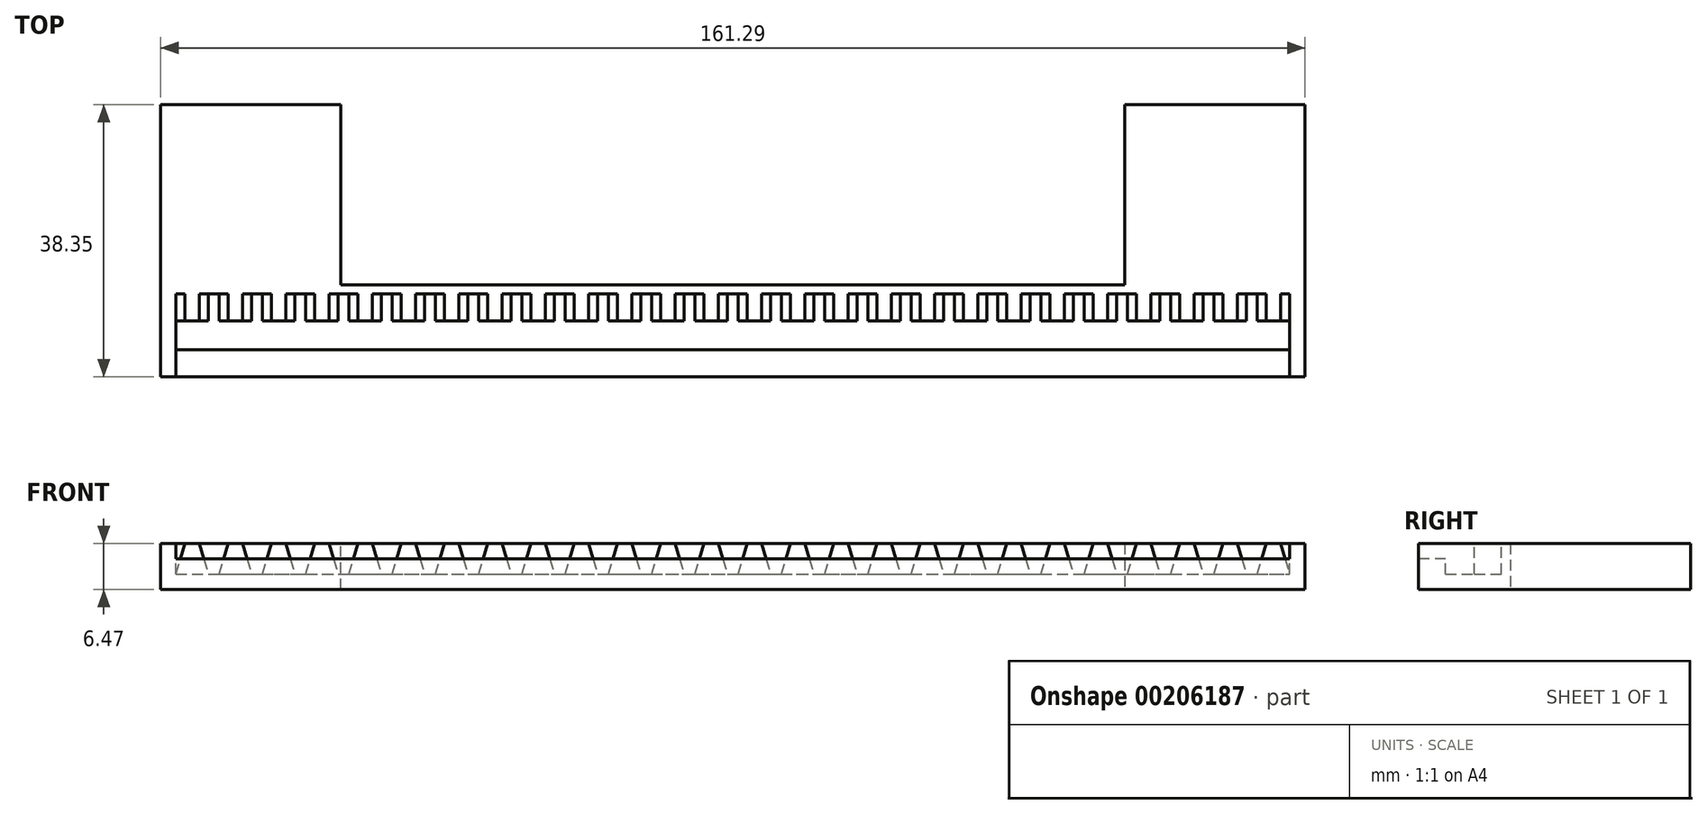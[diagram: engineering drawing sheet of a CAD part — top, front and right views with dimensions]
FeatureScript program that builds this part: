
annotation { "Feature Type Name" : "Feature", "Feature Type Description" : "" }
export const myFeature = defineFeature(function(context is Context, id is Id, definition is map)
    precondition{}
    {
        {
            var Q0;
            Q0=qCreatedBy(makeId("Front.planeOp"),FACE);
            var sketch = newSketch(context, id + "F0", { "sketchPlane" : qUnion([Q0])});
            skLineSegment(sketch, "E0.top", {"start": v(-38.44, 16.9) * mm, "end": v(33.18, 16.9) * mm});
            skLineSegment(sketch, "E0.left", {"start": v(-38.44, 14.74) * mm, "end": v(-38.44, 16.9) * mm});
            skLineSegment(sketch, "E1", {"start": v(-38.44, 16.9) * mm, "end": v(-37.17, 21.21) * mm});
            skLineSegment(sketch, "E2", {"start": v(-37.17, 21.21) * mm, "end": v(-35.14, 21.21) * mm});
            skLineSegment(sketch, "E3", {"start": v(-35.14, 21.21) * mm, "end": v(-33.87, 16.9) * mm});
            skLineSegment(sketch, "E4", {"start": v(-38.44, 16.9) * mm, "end": v(-33.87, 16.9) * mm});
            skLineSegment(sketch, "E5", {"start": v(-36.16, 21.21) * mm, "end": v(-36.16, 16.9) * mm, "construction": true});
            skLineSegment(sketch, "E6.1.0.0", {"start": v(-29.05, 21.21) * mm, "end": v(-27.78, 16.9) * mm});
            skLineSegment(sketch, "E6.1.0.1", {"start": v(-32.35, 16.9) * mm, "end": v(-31.08, 21.21) * mm});
            skLineSegment(sketch, "E6.1.0.2", {"start": v(-31.08, 21.21) * mm, "end": v(-29.05, 21.21) * mm});
            skLineSegment(sketch, "E6.2.0.0", {"start": v(-22.95, 21.21) * mm, "end": v(-21.68, 16.9) * mm});
            skLineSegment(sketch, "E6.2.0.1", {"start": v(-26.25, 16.9) * mm, "end": v(-24.98, 21.21) * mm});
            skLineSegment(sketch, "E6.2.0.2", {"start": v(-24.98, 21.21) * mm, "end": v(-22.95, 21.21) * mm});
            skLineSegment(sketch, "E6.3.0.0", {"start": v(-16.85, 21.21) * mm, "end": v(-15.58, 16.9) * mm});
            skLineSegment(sketch, "E6.3.0.1", {"start": v(-20.16, 16.9) * mm, "end": v(-18.89, 21.21) * mm});
            skLineSegment(sketch, "E6.3.0.2", {"start": v(-18.89, 21.21) * mm, "end": v(-16.85, 21.21) * mm});
            skLineSegment(sketch, "E6.4.0.0", {"start": v(-10.76, 21.21) * mm, "end": v(-9.49, 16.9) * mm});
            skLineSegment(sketch, "E6.4.0.1", {"start": v(-14.06, 16.9) * mm, "end": v(-12.8, 21.21) * mm});
            skLineSegment(sketch, "E6.4.0.2", {"start": v(-12.8, 21.21) * mm, "end": v(-10.76, 21.21) * mm});
            skLineSegment(sketch, "E6.5.0.0", {"start": v(-4.66, 21.21) * mm, "end": v(-3.4, 16.9) * mm});
            skLineSegment(sketch, "E6.5.0.1", {"start": v(-7.96, 16.9) * mm, "end": v(-6.7, 21.21) * mm});
            skLineSegment(sketch, "E6.5.0.2", {"start": v(-6.7, 21.21) * mm, "end": v(-4.66, 21.21) * mm});
            skLineSegment(sketch, "E6.6.0.0", {"start": v(1.43, 21.21) * mm, "end": v(2.7, 16.9) * mm});
            skLineSegment(sketch, "E6.6.0.1", {"start": v(-1.87, 16.9) * mm, "end": v(-0.6, 21.21) * mm});
            skLineSegment(sketch, "E6.6.0.2", {"start": v(-0.6, 21.21) * mm, "end": v(1.43, 21.21) * mm});
            skLineSegment(sketch, "E6.7.0.0", {"start": v(7.53, 21.21) * mm, "end": v(8.8, 16.9) * mm});
            skLineSegment(sketch, "E6.7.0.1", {"start": v(4.23, 16.9) * mm, "end": v(5.5, 21.21) * mm});
            skLineSegment(sketch, "E6.7.0.2", {"start": v(5.5, 21.21) * mm, "end": v(7.53, 21.21) * mm});
            skLineSegment(sketch, "E6.8.0.0", {"start": v(13.63, 21.21) * mm, "end": v(14.9, 16.9) * mm});
            skLineSegment(sketch, "E6.8.0.1", {"start": v(10.32, 16.9) * mm, "end": v(11.6, 21.21) * mm});
            skLineSegment(sketch, "E6.8.0.2", {"start": v(11.6, 21.21) * mm, "end": v(13.63, 21.21) * mm});
            skLineSegment(sketch, "E6.9.0.0", {"start": v(19.72, 21.21) * mm, "end": v(21, 16.9) * mm});
            skLineSegment(sketch, "E6.9.0.1", {"start": v(16.42, 16.9) * mm, "end": v(17.69, 21.21) * mm});
            skLineSegment(sketch, "E6.9.0.2", {"start": v(17.69, 21.21) * mm, "end": v(19.72, 21.21) * mm});
            skLineSegment(sketch, "E6.10.0.0", {"start": v(25.82, 21.21) * mm, "end": v(27.09, 16.9) * mm});
            skLineSegment(sketch, "E6.10.0.1", {"start": v(22.52, 16.9) * mm, "end": v(23.79, 21.21) * mm});
            skLineSegment(sketch, "E6.10.0.2", {"start": v(23.79, 21.21) * mm, "end": v(25.82, 21.21) * mm});
            skLineSegment(sketch, "E6.11.0.0", {"start": v(31.91, 21.21) * mm, "end": v(33.18, 16.9) * mm});
            skLineSegment(sketch, "E6.11.0.1", {"start": v(28.61, 16.9) * mm, "end": v(29.88, 21.21) * mm});
            skLineSegment(sketch, "E6.11.0.2", {"start": v(29.88, 21.21) * mm, "end": v(31.91, 21.21) * mm});
            skLineSegment(sketch, "E6.direction1", {"start": v(-38.44, 16.9) * mm, "end": v(-32.35, 16.9) * mm, "construction": true});
            skPoint(sketch, "E7.centerSnap0", {"position": v(-38.44, 15.82) * mm});
            skLineSegment(sketch, "E8.0.12.0", {"start": v(38, 21.21) * mm, "end": v(39.28, 16.9) * mm});
            skLineSegment(sketch, "E8.3.12.0", {"start": v(34.7, 16.9) * mm, "end": v(35.98, 21.21) * mm});
            skLineSegment(sketch, "E8.6.12.0", {"start": v(35.98, 21.21) * mm, "end": v(38, 21.21) * mm});
            skLineSegment(sketch, "E8.0.13.0", {"start": v(44.1, 21.21) * mm, "end": v(45.38, 16.9) * mm});
            skLineSegment(sketch, "E8.3.13.0", {"start": v(40.8, 16.9) * mm, "end": v(42.07, 21.21) * mm});
            skLineSegment(sketch, "E8.6.13.0", {"start": v(42.07, 21.21) * mm, "end": v(44.1, 21.21) * mm});
            skLineSegment(sketch, "E8.0.14.0", {"start": v(50.2, 21.21) * mm, "end": v(51.47, 16.9) * mm});
            skLineSegment(sketch, "E8.3.14.0", {"start": v(46.9, 16.9) * mm, "end": v(48.17, 21.21) * mm});
            skLineSegment(sketch, "E8.6.14.0", {"start": v(48.17, 21.21) * mm, "end": v(50.2, 21.21) * mm});
            skLineSegment(sketch, "E8.0.15.0", {"start": v(56.3, 21.21) * mm, "end": v(57.57, 16.9) * mm});
            skLineSegment(sketch, "E8.3.15.0", {"start": v(53, 16.9) * mm, "end": v(54.27, 21.21) * mm});
            skLineSegment(sketch, "E8.6.15.0", {"start": v(54.27, 21.21) * mm, "end": v(56.3, 21.21) * mm});
            skLineSegment(sketch, "E8.0.16.0", {"start": v(62.4, 21.21) * mm, "end": v(63.66, 16.9) * mm});
            skLineSegment(sketch, "E8.3.16.0", {"start": v(59.1, 16.9) * mm, "end": v(60.36, 21.21) * mm});
            skLineSegment(sketch, "E8.6.16.0", {"start": v(60.36, 21.21) * mm, "end": v(62.4, 21.21) * mm});
            skLineSegment(sketch, "E8.0.17.0", {"start": v(68.49, 21.21) * mm, "end": v(69.76, 16.9) * mm});
            skLineSegment(sketch, "E8.3.17.0", {"start": v(65.19, 16.9) * mm, "end": v(66.46, 21.21) * mm});
            skLineSegment(sketch, "E8.6.17.0", {"start": v(66.46, 21.21) * mm, "end": v(68.49, 21.21) * mm});
            skLineSegment(sketch, "E9.0.18.0", {"start": v(74.59, 21.21) * mm, "end": v(75.86, 16.9) * mm});
            skLineSegment(sketch, "E9.3.18.0", {"start": v(71.28, 16.9) * mm, "end": v(72.55, 21.21) * mm});
            skLineSegment(sketch, "E9.6.18.0", {"start": v(72.55, 21.21) * mm, "end": v(74.59, 21.21) * mm});
            skLineSegment(sketch, "E9.0.19.0", {"start": v(80.68, 21.21) * mm, "end": v(81.95, 16.9) * mm});
            skLineSegment(sketch, "E9.3.19.0", {"start": v(77.38, 16.9) * mm, "end": v(78.65, 21.21) * mm});
            skLineSegment(sketch, "E9.6.19.0", {"start": v(78.65, 21.21) * mm, "end": v(80.68, 21.21) * mm});
            skLineSegment(sketch, "E10.0.20.0", {"start": v(86.78, 21.21) * mm, "end": v(88.05, 16.9) * mm});
            skLineSegment(sketch, "E10.3.20.0", {"start": v(83.48, 16.9) * mm, "end": v(84.75, 21.21) * mm});
            skLineSegment(sketch, "E10.6.20.0", {"start": v(84.75, 21.21) * mm, "end": v(86.78, 21.21) * mm});
            skLineSegment(sketch, "E10.0.21.0", {"start": v(92.87, 21.21) * mm, "end": v(94.14, 16.9) * mm});
            skLineSegment(sketch, "E10.3.21.0", {"start": v(89.57, 16.9) * mm, "end": v(90.84, 21.21) * mm});
            skLineSegment(sketch, "E10.6.21.0", {"start": v(90.84, 21.21) * mm, "end": v(92.87, 21.21) * mm});
            skLineSegment(sketch, "E10.0.22.0", {"start": v(98.97, 21.21) * mm, "end": v(100.24, 16.9) * mm});
            skLineSegment(sketch, "E10.3.22.0", {"start": v(95.67, 16.9) * mm, "end": v(96.94, 21.21) * mm});
            skLineSegment(sketch, "E10.6.22.0", {"start": v(96.94, 21.21) * mm, "end": v(98.97, 21.21) * mm});
            skLineSegment(sketch, "E10.0.23.0", {"start": v(105.07, 21.21) * mm, "end": v(106.34, 16.9) * mm});
            skLineSegment(sketch, "E10.3.23.0", {"start": v(101.76, 16.9) * mm, "end": v(103.03, 21.21) * mm});
            skLineSegment(sketch, "E10.6.23.0", {"start": v(103.03, 21.21) * mm, "end": v(105.07, 21.21) * mm});
            skLineSegment(sketch, "E11.0.24.0", {"start": v(111.16, 21.21) * mm, "end": v(112.43, 16.9) * mm});
            skLineSegment(sketch, "E11.3.24.0", {"start": v(107.86, 16.9) * mm, "end": v(109.13, 21.21) * mm});
            skLineSegment(sketch, "E11.6.24.0", {"start": v(109.13, 21.21) * mm, "end": v(111.16, 21.21) * mm});
            skLineSegment(sketch, "E12.0.25.0", {"start": v(117.26, 21.21) * mm, "end": v(118.53, 16.9) * mm});
            skLineSegment(sketch, "E12.3.25.0", {"start": v(113.96, 16.9) * mm, "end": v(115.23, 21.21) * mm});
            skLineSegment(sketch, "E12.6.25.0", {"start": v(115.23, 21.21) * mm, "end": v(117.26, 21.21) * mm});
            skLineSegment(sketch, "E13", {"start": v(33.18, 16.9) * mm, "end": v(118.53, 16.9) * mm});
            skLineSegment(sketch, "E14", {"start": v(-38.44, 14.74) * mm, "end": v(118.53, 14.74) * mm});
            skLineSegment(sketch, "E15", {"start": v(118.53, 14.74) * mm, "end": v(118.53, 16.9) * mm});
            skSolve(sketch);
        }
        {
            var Q0;
            Q0=qSketchRegion(id+"F0",true);
            extrude(context, id + "F1", {"entities" : qUnion([Q0]), "depth" : 3.8 * mm});
        }
        {
            var Q0;
            Q0=makeQuery(id+"F1.opExtrude","SWEPT_EDGE",EDGE,{"disambiguationData":[OSD([sQuery(id+"F0.wireOp",EDGE,"E14"),sQuery(id+"F0.wireOp",EDGE,"E15")])]});
            cPoint(context, id + "F2", {"entities" : qUnion([Q0]), "parameter" : 0.5});
        }
        {
            var Q0;
            Q0=qCreatedBy(makeId("Right.planeOp"),FACE);
            var Q1;
            Q1=qCreatedBy(id+"F2",VERTEX);
            cPlane(context, id + "F3", {"entities" : qUnion([Q0, Q1]), "cplaneType" : CPlaneType.PLANE_POINT, "offset" : 25.4 * mm, "width" : 152.4 * mm, "height" : 152.4 * mm});
        }
        {
            var Q0;
            Q0=qCreatedBy(id+"F3.planeOp",FACE);
            var sketch = newSketch(context, id + "F4", { "sketchPlane" : qUnion([Q0])});
            skLineSegment(sketch, "E16.0", {"start": v(-3.81, 14.74) * mm, "end": v(-3.81, 16.9) * mm});
            skLineSegment(sketch, "E17", {"start": v(-15.5, 16.9) * mm, "end": v(-11.68, 16.9) * mm});
            skLineSegment(sketch, "E18", {"start": v(-7.87, 16.9) * mm, "end": v(-7.87, 19.05) * mm});
            skLineSegment(sketch, "E19", {"start": v(-7.87, 19.05) * mm, "end": v(-11.68, 19.05) * mm});
            skLineSegment(sketch, "E20", {"start": v(-11.68, 19.05) * mm, "end": v(-11.68, 16.9) * mm});
            skLineSegment(sketch, "E21.trimOffspring", {"start": v(-7.87, 16.9) * mm, "end": v(-3.81, 16.9) * mm});
            skLineSegment(sketch, "E22", {"start": v(-3.81, 14.74) * mm, "end": v(-15.5, 14.74) * mm});
            skLineSegment(sketch, "E23", {"start": v(-15.5, 14.74) * mm, "end": v(-15.5, 16.9) * mm});
            skLineSegment(sketch, "E24", {"start": v(-11.68, 16.9) * mm, "end": v(-11.68, 14.74) * mm});
            skSolve(sketch);
        }
        {
            var Q0;
            {var subQ0=sQuery(id+"F4.wireOp",EDGE,"E16.0");Q0=makeQuery(id+"F4.imprint","IMPRINT",FACE,{"disambiguationData":[TD([[makeQuery(id+"F4.imprint","IMPRINT",EDGE,{"derivedFrom":subQ0}),1.0]])]});}
            var Q1;
            Q1=makeQuery(id+"F1.opExtrude","SWEPT_FACE",FACE,{"disambiguationData":[OSD([sQuery(id+"F0.wireOp",EDGE,"E0.left")])]});
            extrude(context, id + "F5", {"entities" : qUnion([Q0]), "operationType" : NewBodyOperationType.ADD, "endBound" : BoundingType.UP_TO_SURFACE, "oppositeDirection" : true, "endBoundEntityFace" : qUnion([Q1]), "depth" : 33.02 * mm});
        }
        {
            var Q0;
            Q0=makeQuery(id+"F1.opExtrude","CAP_FACE",FACE,{"disambiguationData":[OSD([sQuery(id+"F0.wireOp",EDGE,"E0.bottom"),sQuery(id+"F0.wireOp",EDGE,"E0.top"),sQuery(id+"F0.wireOp",EDGE,"E0.left"),sQuery(id+"F0.wireOp",EDGE,"E1"),sQuery(id+"F0.wireOp",EDGE,"E2"),sQuery(id+"F0.wireOp",EDGE,"E3"),sQuery(id+"F0.wireOp",EDGE,"9qWjWlUo-ttb5-mKxR-HVll-tsb38tv3fsYN"),sQuery(id+"F0.wireOp",EDGE,"E6.1.0.0"),sQuery(id+"F0.wireOp",EDGE,"E6.1.0.1"),sQuery(id+"F0.wireOp",EDGE,"E6.1.0.2"),sQuery(id+"F0.wireOp",EDGE,"E6.2.0.0"),sQuery(id+"F0.wireOp",EDGE,"E6.2.0.1"),sQuery(id+"F0.wireOp",EDGE,"E6.2.0.2"),sQuery(id+"F0.wireOp",EDGE,"E6.3.0.0"),sQuery(id+"F0.wireOp",EDGE,"E6.3.0.1"),sQuery(id+"F0.wireOp",EDGE,"E6.3.0.2"),sQuery(id+"F0.wireOp",EDGE,"E6.4.0.0"),sQuery(id+"F0.wireOp",EDGE,"E6.4.0.1"),sQuery(id+"F0.wireOp",EDGE,"E6.4.0.2"),sQuery(id+"F0.wireOp",EDGE,"E6.5.0.0"),sQuery(id+"F0.wireOp",EDGE,"E6.5.0.1"),sQuery(id+"F0.wireOp",EDGE,"E6.5.0.2"),sQuery(id+"F0.wireOp",EDGE,"E6.6.0.0"),sQuery(id+"F0.wireOp",EDGE,"E6.6.0.1"),sQuery(id+"F0.wireOp",EDGE,"E6.6.0.2"),sQuery(id+"F0.wireOp",EDGE,"E6.7.0.0"),sQuery(id+"F0.wireOp",EDGE,"E6.7.0.1"),sQuery(id+"F0.wireOp",EDGE,"E6.7.0.2"),sQuery(id+"F0.wireOp",EDGE,"E6.8.0.0"),sQuery(id+"F0.wireOp",EDGE,"E6.8.0.1"),sQuery(id+"F0.wireOp",EDGE,"E6.8.0.2"),sQuery(id+"F0.wireOp",EDGE,"E6.9.0.0"),sQuery(id+"F0.wireOp",EDGE,"E6.9.0.1"),sQuery(id+"F0.wireOp",EDGE,"E6.9.0.2"),sQuery(id+"F0.wireOp",EDGE,"E6.10.0.0"),sQuery(id+"F0.wireOp",EDGE,"E6.10.0.1"),sQuery(id+"F0.wireOp",EDGE,"E6.10.0.2"),sQuery(id+"F0.wireOp",EDGE,"E6.11.0.0"),sQuery(id+"F0.wireOp",EDGE,"E6.11.0.1"),sQuery(id+"F0.wireOp",EDGE,"E6.11.0.2")])],"isStart":true});
            var sketch = newSketch(context, id + "F6", { "sketchPlane" : qUnion([Q0])});
            skPoint(sketch, "E25.oppositeSnap0", {"position": v(23.97, 21.21) * mm});
            skLineSegment(sketch, "E25.bottom", {"start": v(38.44, 14.74) * mm, "end": v(-118.53, 14.74) * mm});
            skLineSegment(sketch, "E25.top", {"start": v(38.44, 21.21) * mm, "end": v(-118.53, 21.21) * mm});
            skLineSegment(sketch, "E25.left", {"start": v(38.44, 14.74) * mm, "end": v(38.44, 21.21) * mm});
            skLineSegment(sketch, "E25.right", {"start": v(-118.53, 14.74) * mm, "end": v(-118.53, 21.21) * mm});
            skLineSegment(sketch, "E26.0", {"start": v(38.44, 16.9) * mm, "end": v(37.17, 21.21) * mm});
            skLineSegment(sketch, "E27.0", {"start": v(-117.26, 21.21) * mm, "end": v(-118.53, 16.9) * mm});
            skSolve(sketch);
        }
        {
            var Q0;
            {var subQ1=sQuery(id+"F0.wireOp",EDGE,"E3");var subQ2=makeQuery(id+"F1.opExtrude","CAP_EDGE",EDGE,{"disambiguationData":[OSD([subQ1])],"isStart":true});Q0=makeQuery(id+"F6.imprint","IMPRINT",FACE,{"disambiguationData":[TD([[makeQuery(id+"F6.imprint","IMPRINT",EDGE,{"derivedFrom":subQ2}),-1.0]])]});}
            var Q1;
            {var subQ1=sQuery(id+"F0.wireOp",EDGE,"E6.1.0.0");var subQ2=makeQuery(id+"F1.opExtrude","CAP_EDGE",EDGE,{"disambiguationData":[OSD([subQ1])],"isStart":true});Q1=makeQuery(id+"F6.imprint","IMPRINT",FACE,{"disambiguationData":[TD([[makeQuery(id+"F6.imprint","IMPRINT",EDGE,{"derivedFrom":subQ2}),-1.0]])]});}
            var Q2;
            {var subQ1=sQuery(id+"F0.wireOp",EDGE,"E6.2.0.0");var subQ2=makeQuery(id+"F1.opExtrude","CAP_EDGE",EDGE,{"disambiguationData":[OSD([subQ1])],"isStart":true});Q2=makeQuery(id+"F6.imprint","IMPRINT",FACE,{"disambiguationData":[TD([[makeQuery(id+"F6.imprint","IMPRINT",EDGE,{"derivedFrom":subQ2}),-1.0]])]});}
            var Q3;
            {var subQ1=sQuery(id+"F0.wireOp",EDGE,"E6.3.0.0");var subQ2=makeQuery(id+"F1.opExtrude","CAP_EDGE",EDGE,{"disambiguationData":[OSD([subQ1])],"isStart":true});Q3=makeQuery(id+"F6.imprint","IMPRINT",FACE,{"disambiguationData":[TD([[makeQuery(id+"F6.imprint","IMPRINT",EDGE,{"derivedFrom":subQ2}),-1.0]])]});}
            var Q4;
            {var subQ1=sQuery(id+"F0.wireOp",EDGE,"E6.4.0.0");var subQ2=makeQuery(id+"F1.opExtrude","CAP_EDGE",EDGE,{"disambiguationData":[OSD([subQ1])],"isStart":true});Q4=makeQuery(id+"F6.imprint","IMPRINT",FACE,{"disambiguationData":[TD([[makeQuery(id+"F6.imprint","IMPRINT",EDGE,{"derivedFrom":subQ2}),-1.0]])]});}
            var Q5;
            {var subQ1=sQuery(id+"F0.wireOp",EDGE,"E6.5.0.0");var subQ2=makeQuery(id+"F1.opExtrude","CAP_EDGE",EDGE,{"disambiguationData":[OSD([subQ1])],"isStart":true});Q5=makeQuery(id+"F6.imprint","IMPRINT",FACE,{"disambiguationData":[TD([[makeQuery(id+"F6.imprint","IMPRINT",EDGE,{"derivedFrom":subQ2}),-1.0]])]});}
            var Q6;
            {var subQ1=sQuery(id+"F0.wireOp",EDGE,"E6.6.0.0");var subQ2=makeQuery(id+"F1.opExtrude","CAP_EDGE",EDGE,{"disambiguationData":[OSD([subQ1])],"isStart":true});Q6=makeQuery(id+"F6.imprint","IMPRINT",FACE,{"disambiguationData":[TD([[makeQuery(id+"F6.imprint","IMPRINT",EDGE,{"derivedFrom":subQ2}),-1.0]])]});}
            var Q7;
            {var subQ1=sQuery(id+"F0.wireOp",EDGE,"E6.7.0.0");var subQ2=makeQuery(id+"F1.opExtrude","CAP_EDGE",EDGE,{"disambiguationData":[OSD([subQ1])],"isStart":true});Q7=makeQuery(id+"F6.imprint","IMPRINT",FACE,{"disambiguationData":[TD([[makeQuery(id+"F6.imprint","IMPRINT",EDGE,{"derivedFrom":subQ2}),-1.0]])]});}
            var Q8;
            {var subQ1=sQuery(id+"F0.wireOp",EDGE,"E6.8.0.0");var subQ2=makeQuery(id+"F1.opExtrude","CAP_EDGE",EDGE,{"disambiguationData":[OSD([subQ1])],"isStart":true});Q8=makeQuery(id+"F6.imprint","IMPRINT",FACE,{"disambiguationData":[TD([[makeQuery(id+"F6.imprint","IMPRINT",EDGE,{"derivedFrom":subQ2}),-1.0]])]});}
            var Q9;
            {var subQ1=sQuery(id+"F0.wireOp",EDGE,"E6.9.0.0");var subQ2=makeQuery(id+"F1.opExtrude","CAP_EDGE",EDGE,{"disambiguationData":[OSD([subQ1])],"isStart":true});Q9=makeQuery(id+"F6.imprint","IMPRINT",FACE,{"disambiguationData":[TD([[makeQuery(id+"F6.imprint","IMPRINT",EDGE,{"derivedFrom":subQ2}),-1.0]])]});}
            var Q10;
            {var subQ1=sQuery(id+"F0.wireOp",EDGE,"E6.10.0.0");var subQ2=makeQuery(id+"F1.opExtrude","CAP_EDGE",EDGE,{"disambiguationData":[OSD([subQ1])],"isStart":true});Q10=makeQuery(id+"F6.imprint","IMPRINT",FACE,{"disambiguationData":[TD([[makeQuery(id+"F6.imprint","IMPRINT",EDGE,{"derivedFrom":subQ2}),-1.0]])]});}
            var Q11;
            {var subQ42=sQuery(id+"F6.wireOp",EDGE,"E25.bottom");Q11=makeQuery(id+"F6.imprint","IMPRINT",FACE,{"disambiguationData":[TD([[makeQuery(id+"F6.imprint","IMPRINT",EDGE,{"derivedFrom":subQ42}),-1.0]])]});}
            var Q12;
            {var subQ1=sQuery(id+"F0.wireOp",EDGE,"E11.0.24.0");var subQ2=makeQuery(id+"F1.opExtrude","CAP_EDGE",EDGE,{"disambiguationData":[OSD([subQ1])],"isStart":true});Q12=makeQuery(id+"F6.imprint","IMPRINT",FACE,{"disambiguationData":[TD([[makeQuery(id+"F6.imprint","IMPRINT",EDGE,{"derivedFrom":subQ2}),-1.0]])]});}
            var Q13;
            {var subQ1=sQuery(id+"F0.wireOp",EDGE,"E10.0.23.0");var subQ2=makeQuery(id+"F1.opExtrude","CAP_EDGE",EDGE,{"disambiguationData":[OSD([subQ1])],"isStart":true});Q13=makeQuery(id+"F6.imprint","IMPRINT",FACE,{"disambiguationData":[TD([[makeQuery(id+"F6.imprint","IMPRINT",EDGE,{"derivedFrom":subQ2}),-1.0]])]});}
            var Q14;
            {var subQ1=sQuery(id+"F0.wireOp",EDGE,"E10.0.22.0");var subQ2=makeQuery(id+"F1.opExtrude","CAP_EDGE",EDGE,{"disambiguationData":[OSD([subQ1])],"isStart":true});Q14=makeQuery(id+"F6.imprint","IMPRINT",FACE,{"disambiguationData":[TD([[makeQuery(id+"F6.imprint","IMPRINT",EDGE,{"derivedFrom":subQ2}),-1.0]])]});}
            var Q15;
            {var subQ1=sQuery(id+"F0.wireOp",EDGE,"E10.0.21.0");var subQ2=makeQuery(id+"F1.opExtrude","CAP_EDGE",EDGE,{"disambiguationData":[OSD([subQ1])],"isStart":true});Q15=makeQuery(id+"F6.imprint","IMPRINT",FACE,{"disambiguationData":[TD([[makeQuery(id+"F6.imprint","IMPRINT",EDGE,{"derivedFrom":subQ2}),-1.0]])]});}
            var Q16;
            {var subQ1=sQuery(id+"F0.wireOp",EDGE,"E10.0.20.0");var subQ2=makeQuery(id+"F1.opExtrude","CAP_EDGE",EDGE,{"disambiguationData":[OSD([subQ1])],"isStart":true});Q16=makeQuery(id+"F6.imprint","IMPRINT",FACE,{"disambiguationData":[TD([[makeQuery(id+"F6.imprint","IMPRINT",EDGE,{"derivedFrom":subQ2}),-1.0]])]});}
            var Q17;
            {var subQ1=sQuery(id+"F0.wireOp",EDGE,"E9.0.19.0");var subQ2=makeQuery(id+"F1.opExtrude","CAP_EDGE",EDGE,{"disambiguationData":[OSD([subQ1])],"isStart":true});Q17=makeQuery(id+"F6.imprint","IMPRINT",FACE,{"disambiguationData":[TD([[makeQuery(id+"F6.imprint","IMPRINT",EDGE,{"derivedFrom":subQ2}),-1.0]])]});}
            var Q18;
            {var subQ1=sQuery(id+"F0.wireOp",EDGE,"E9.0.18.0");var subQ2=makeQuery(id+"F1.opExtrude","CAP_EDGE",EDGE,{"disambiguationData":[OSD([subQ1])],"isStart":true});Q18=makeQuery(id+"F6.imprint","IMPRINT",FACE,{"disambiguationData":[TD([[makeQuery(id+"F6.imprint","IMPRINT",EDGE,{"derivedFrom":subQ2}),-1.0]])]});}
            var Q19;
            {var subQ1=sQuery(id+"F0.wireOp",EDGE,"E8.0.17.0");var subQ2=makeQuery(id+"F1.opExtrude","CAP_EDGE",EDGE,{"disambiguationData":[OSD([subQ1])],"isStart":true});Q19=makeQuery(id+"F6.imprint","IMPRINT",FACE,{"disambiguationData":[TD([[makeQuery(id+"F6.imprint","IMPRINT",EDGE,{"derivedFrom":subQ2}),-1.0]])]});}
            var Q20;
            {var subQ1=sQuery(id+"F0.wireOp",EDGE,"E8.0.16.0");var subQ2=makeQuery(id+"F1.opExtrude","CAP_EDGE",EDGE,{"disambiguationData":[OSD([subQ1])],"isStart":true});Q20=makeQuery(id+"F6.imprint","IMPRINT",FACE,{"disambiguationData":[TD([[makeQuery(id+"F6.imprint","IMPRINT",EDGE,{"derivedFrom":subQ2}),-1.0]])]});}
            var Q21;
            {var subQ1=sQuery(id+"F0.wireOp",EDGE,"E8.0.15.0");var subQ2=makeQuery(id+"F1.opExtrude","CAP_EDGE",EDGE,{"disambiguationData":[OSD([subQ1])],"isStart":true});Q21=makeQuery(id+"F6.imprint","IMPRINT",FACE,{"disambiguationData":[TD([[makeQuery(id+"F6.imprint","IMPRINT",EDGE,{"derivedFrom":subQ2}),-1.0]])]});}
            var Q22;
            {var subQ1=sQuery(id+"F0.wireOp",EDGE,"E8.0.14.0");var subQ2=makeQuery(id+"F1.opExtrude","CAP_EDGE",EDGE,{"disambiguationData":[OSD([subQ1])],"isStart":true});Q22=makeQuery(id+"F6.imprint","IMPRINT",FACE,{"disambiguationData":[TD([[makeQuery(id+"F6.imprint","IMPRINT",EDGE,{"derivedFrom":subQ2}),-1.0]])]});}
            var Q23;
            {var subQ1=sQuery(id+"F0.wireOp",EDGE,"E8.0.13.0");var subQ2=makeQuery(id+"F1.opExtrude","CAP_EDGE",EDGE,{"disambiguationData":[OSD([subQ1])],"isStart":true});Q23=makeQuery(id+"F6.imprint","IMPRINT",FACE,{"disambiguationData":[TD([[makeQuery(id+"F6.imprint","IMPRINT",EDGE,{"derivedFrom":subQ2}),-1.0]])]});}
            var Q24;
            {var subQ1=sQuery(id+"F0.wireOp",EDGE,"E8.0.12.0");var subQ2=makeQuery(id+"F1.opExtrude","CAP_EDGE",EDGE,{"disambiguationData":[OSD([subQ1])],"isStart":true});Q24=makeQuery(id+"F6.imprint","IMPRINT",FACE,{"disambiguationData":[TD([[makeQuery(id+"F6.imprint","IMPRINT",EDGE,{"derivedFrom":subQ2}),-1.0]])]});}
            var Q25;
            {var subQ1=sQuery(id+"F0.wireOp",EDGE,"E6.11.0.0");var subQ2=makeQuery(id+"F1.opExtrude","CAP_EDGE",EDGE,{"disambiguationData":[OSD([subQ1])],"isStart":true});Q25=makeQuery(id+"F6.imprint","IMPRINT",FACE,{"disambiguationData":[TD([[makeQuery(id+"F6.imprint","IMPRINT",EDGE,{"derivedFrom":subQ2}),-1.0]])]});}
            var Q26;
            {var subQ0=sQuery(id+"F6.wireOp",EDGE,"E27.0");Q26=makeQuery(id+"F6.imprint","IMPRINT",FACE,{"disambiguationData":[TD([[makeQuery(id+"F6.imprint","IMPRINT",EDGE,{"derivedFrom":subQ0}),-1.0]])]});}
            var Q27;
            {var subQ0=sQuery(id+"F6.wireOp",EDGE,"E26.0");Q27=makeQuery(id+"F6.imprint","IMPRINT",FACE,{"disambiguationData":[TD([[makeQuery(id+"F6.imprint","IMPRINT",EDGE,{"derivedFrom":subQ0}),-1.0]])]});}
            extrude(context, id + "F7", {"entities" : qUnion([Q0, Q1, Q2, Q3, Q4, Q5, Q6, Q7, Q8, Q9, Q10, Q11, Q12, Q13, Q14, Q15, Q16, Q17, Q18, Q19, Q20, Q21, Q22, Q23, Q24, Q25, Q26, Q27]), "operationType" : NewBodyOperationType.ADD, "depth" : 1.27 * mm});
        }
        {
            var Q0;
            Q0=makeQuery(id+"F7.boolean.opBoolean","MERGE",FACE,{"derivedFrom":[makeQuery(id+"F5.boolean.opBoolean","MERGE",FACE,{"derivedFrom":[makeQuery(id+"F1.opExtrude","SWEPT_FACE",FACE,{"disambiguationData":[OSD([sQuery(id+"F0.wireOp",EDGE,"E15")])]}),makeQuery(id+"F5.opExtrude","CAP_FACE",FACE,{"disambiguationData":[OSD([sQuery(id+"F4.wireOp",EDGE,"E16.0"),sQuery(id+"F4.wireOp",EDGE,"E18"),sQuery(id+"F4.wireOp",EDGE,"E19"),sQuery(id+"F4.wireOp",EDGE,"E20"),sQuery(id+"F4.wireOp",EDGE,"E21.trimOffspring"),sQuery(id+"F4.wireOp",EDGE,"E22"),sQuery(id+"F4.wireOp",EDGE,"E24")])],"isStart":true})]}),makeQuery(id+"F7.opExtrude","SWEPT_FACE",FACE,{"disambiguationData":[OSD([sQuery(id+"F6.wireOp",EDGE,"E25.right")])]})]});
            var sketch = newSketch(context, id + "F9", { "sketchPlane" : qUnion([Q0])});
            skLineSegment(sketch, "E28.bottom", {"start": v(-11.68, 14.74) * mm, "end": v(1.27, 14.74) * mm});
            skLineSegment(sketch, "E28.top", {"start": v(-11.68, 21.21) * mm, "end": v(1.27, 21.21) * mm});
            skLineSegment(sketch, "E28.left", {"start": v(-11.68, 14.74) * mm, "end": v(-11.68, 21.21) * mm});
            skLineSegment(sketch, "E28.right", {"start": v(1.27, 14.74) * mm, "end": v(1.27, 21.21) * mm});
            skLineSegment(sketch, "E29.top", {"start": v(-11.68, 16.9) * mm, "end": v(1.27, 16.9) * mm});
            skLineSegment(sketch, "E29.left", {"start": v(-11.68, 14.74) * mm, "end": v(-11.68, 16.9) * mm});
            skLineSegment(sketch, "E29.right", {"start": v(1.27, 14.74) * mm, "end": v(1.27, 16.9) * mm});
            skSolve(sketch);
        }
        {
            var Q0;
            Q0=qSketchRegion(id+"F9",true);
            extrude(context, id + "F10", {"entities" : qUnion([Q0]), "operationType" : NewBodyOperationType.ADD, "depth" : 2.16 * mm});
        }
        {
            var Q0;
            {var subQ0=sQuery(id+"F0.wireOp",EDGE,"E0.left");Q0=makeQuery(id+"F7.boolean.opBoolean","MERGE",FACE,{"derivedFrom":[makeQuery(id+"F5.boolean.opBoolean","MERGE",FACE,{"derivedFrom":[makeQuery(id+"F1.opExtrude","SWEPT_FACE",FACE,{"disambiguationData":[OSD([subQ0])]}),makeQuery(id+"F5.opExtrude","CAP_FACE",FACE,{"disambiguationData":[OSD([subQ0])],"isStart":false})]}),makeQuery(id+"F7.opExtrude","SWEPT_FACE",FACE,{"disambiguationData":[OSD([sQuery(id+"F6.wireOp",EDGE,"E25.left")])]})]});}
            var sketch = newSketch(context, id + "F11", { "sketchPlane" : qUnion([Q0])});
            skLineSegment(sketch, "E30.0", {"start": v(11.68, 21.21) * mm, "end": v(-1.27, 21.21) * mm});
            skLineSegment(sketch, "E31.bottom", {"start": v(11.68, 14.74) * mm, "end": v(-1.27, 14.74) * mm});
            skLineSegment(sketch, "E31.left", {"start": v(11.68, 14.74) * mm, "end": v(11.68, 21.21) * mm});
            skLineSegment(sketch, "E31.right", {"start": v(-1.27, 14.74) * mm, "end": v(-1.27, 21.21) * mm});
            skLineSegment(sketch, "E32.left", {"start": v(11.68, 14.74) * mm, "end": v(11.68, 14.74) * mm});
            skLineSegment(sketch, "E32.right", {"start": v(-1.27, 14.74) * mm, "end": v(-1.27, 14.74) * mm});
            skPoint(sketch, "E33.oppositeSnap0", {"position": v(-1.27, 17.97) * mm});
            skLineSegment(sketch, "E33.top", {"start": v(11.68, 16.9) * mm, "end": v(-1.27, 16.9) * mm});
            skLineSegment(sketch, "E33.left", {"start": v(11.68, 14.74) * mm, "end": v(11.68, 16.9) * mm});
            skLineSegment(sketch, "E33.right", {"start": v(-1.27, 14.74) * mm, "end": v(-1.27, 16.9) * mm});
            skSolve(sketch);
        }
        {
            var Q0;
            Q0=qSketchRegion(id+"F11",true);
            extrude(context, id + "F12", {"entities" : qUnion([Q0]), "operationType" : NewBodyOperationType.ADD, "depth" : 2.16 * mm});
        }
        {
            var Q0;
            Q0=makeQuery(id+"F12.boolean.opBoolean","MERGE",FACE,{"derivedFrom":[makeQuery(id+"F10.boolean.opBoolean","MERGE",FACE,{"derivedFrom":[makeQuery(id+"F7.opExtrude","CAP_FACE",FACE,{"disambiguationData":[OSD([sQuery(id+"F6.wireOp",EDGE,"E25.bottom"),sQuery(id+"F6.wireOp",EDGE,"E25.top"),sQuery(id+"F6.wireOp",EDGE,"E25.left"),sQuery(id+"F6.wireOp",EDGE,"E25.right")])],"isStart":false}),makeQuery(id+"F10.opExtrude","SWEPT_FACE",FACE,{"disambiguationData":[OSD([sQuery(id+"F9.wireOp",EDGE,"E28.right"),sQuery(id+"F9.wireOp",EDGE,"E29.right")])]})]}),makeQuery(id+"F12.opExtrude","SWEPT_FACE",FACE,{"disambiguationData":[OSD([sQuery(id+"F11.wireOp",EDGE,"E31.right"),sQuery(id+"F11.wireOp",EDGE,"E33.right")])]})]});
            var sketch = newSketch(context, id + "F13", { "sketchPlane" : qUnion([Q0])});
            skLineSegment(sketch, "E34.bottom", {"start": v(40.6, 14.74) * mm, "end": v(15.2, 14.74) * mm});
            skLineSegment(sketch, "E34.top", {"start": v(40.6, 21.21) * mm, "end": v(15.2, 21.21) * mm});
            skLineSegment(sketch, "E34.left", {"start": v(40.6, 14.74) * mm, "end": v(40.6, 21.21) * mm});
            skLineSegment(sketch, "E34.right", {"start": v(15.2, 14.74) * mm, "end": v(15.2, 21.21) * mm});
            skLineSegment(sketch, "E35.bottom", {"start": v(-120.69, 21.21) * mm, "end": v(-95.29, 21.21) * mm});
            skLineSegment(sketch, "E35.top", {"start": v(-120.69, 14.74) * mm, "end": v(-95.29, 14.74) * mm});
            skLineSegment(sketch, "E35.left", {"start": v(-120.69, 21.21) * mm, "end": v(-120.69, 14.74) * mm});
            skLineSegment(sketch, "E35.right", {"start": v(-95.29, 21.21) * mm, "end": v(-95.29, 14.74) * mm});
            skSolve(sketch);
        }
        {
            var Q0;
            Q0=qSketchRegion(id+"F13",true);
            extrude(context, id + "F14", {"entities" : qUnion([Q0]), "operationType" : NewBodyOperationType.ADD, "depth" : 25.4 * mm});
        }
    });
